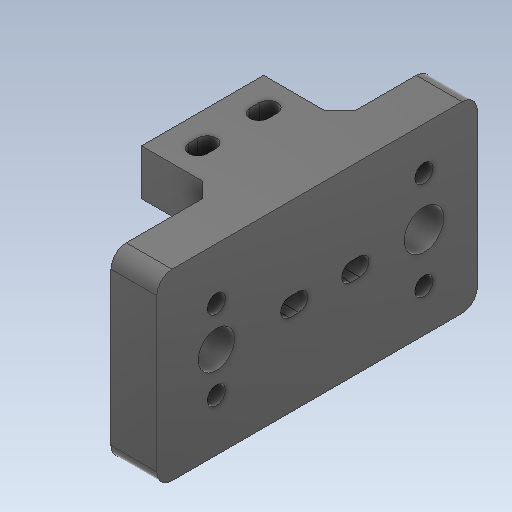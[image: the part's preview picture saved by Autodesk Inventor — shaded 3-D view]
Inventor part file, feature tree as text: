
AUTODESK INVENTOR PART (.ipt)
format: ipt  version: 2020 (Build 240168000, 168)  size: 249,344 bytes
history: native  units: mm
features: extrude x7, sketch x7, chamfer x1, fillet x1, mirror x1
ambient origin geometry x8: Origin, YZ Plane, XZ Plane, XY Plane, X Axis, Y Axis, Z Axis, Center Point
bodies: Solid1 (feature_tree)
feature tree (17):
  extrude  "Extrusion1"  Depth=40.0mm
  extrude  "Extrusion2"  Depth=40.0mm TaperAngle=0.0deg
  extrude  "Extrusion3"  Depth=3.0mm
  extrude  "Extrusion4"  Depth=30.0mm
  extrude  "Extrusion5"  Depth=3.0mm
  extrude  "Extrusion6"  Depth=10.0mm
  extrude  "Extrusion7"  TaperAngle=0.0deg  [1 undecoded]
  chamfer  "Chamfer2"  Distance=30.0mm
  fillet  "Fillet2"  Radius=32.0mm
  mirror  "Mirror1"
  sketch  "Sketch1"  dims[d0=15.0mm d1=40.0mm]
  sketch  "Sketch2"  dims[d2=60.0mm d3=40.0mm d4=0.0mm]
  sketch  "Sketch3"  dims[d5=6.0mm d6=3.0mm]
  sketch  "Sketch5"  dims[d7=10.0mm d8=30.0mm]
  sketch  "Sketch6"  dims[d9=0.0mm d10=0.0mm d11=3.0mm]
  sketch  "Sketch7"  dims[d12=6.0mm d13=10.0mm]
  sketch  "Sketch8"  dims[d14=10.0mm d15=0.0mm d16=0.0mm d21=30.0mm d22=0.0mm d23=32.0mm d24=14.0mm d25=17.5mm d26=6.0mm d27=0.0mm d28=0.0mm d29=35.0mm d30=0.0mm d31=13.0mm d32=16.0mm d33=12.0mm d34=6.0mm d35=17.0mm d36=19.5mm d37=26.0mm d38=13.0mm d39=0.0mm d40=0.0mm d41=5.0mm d42=2.0mm d43=45.0deg d44=5.0mm]
note: 1 required parameter value undecoded (feature->parameter linkage not recoverable at this tier; creation-order binding heuristic only, values carry confidence <= 0.55)
